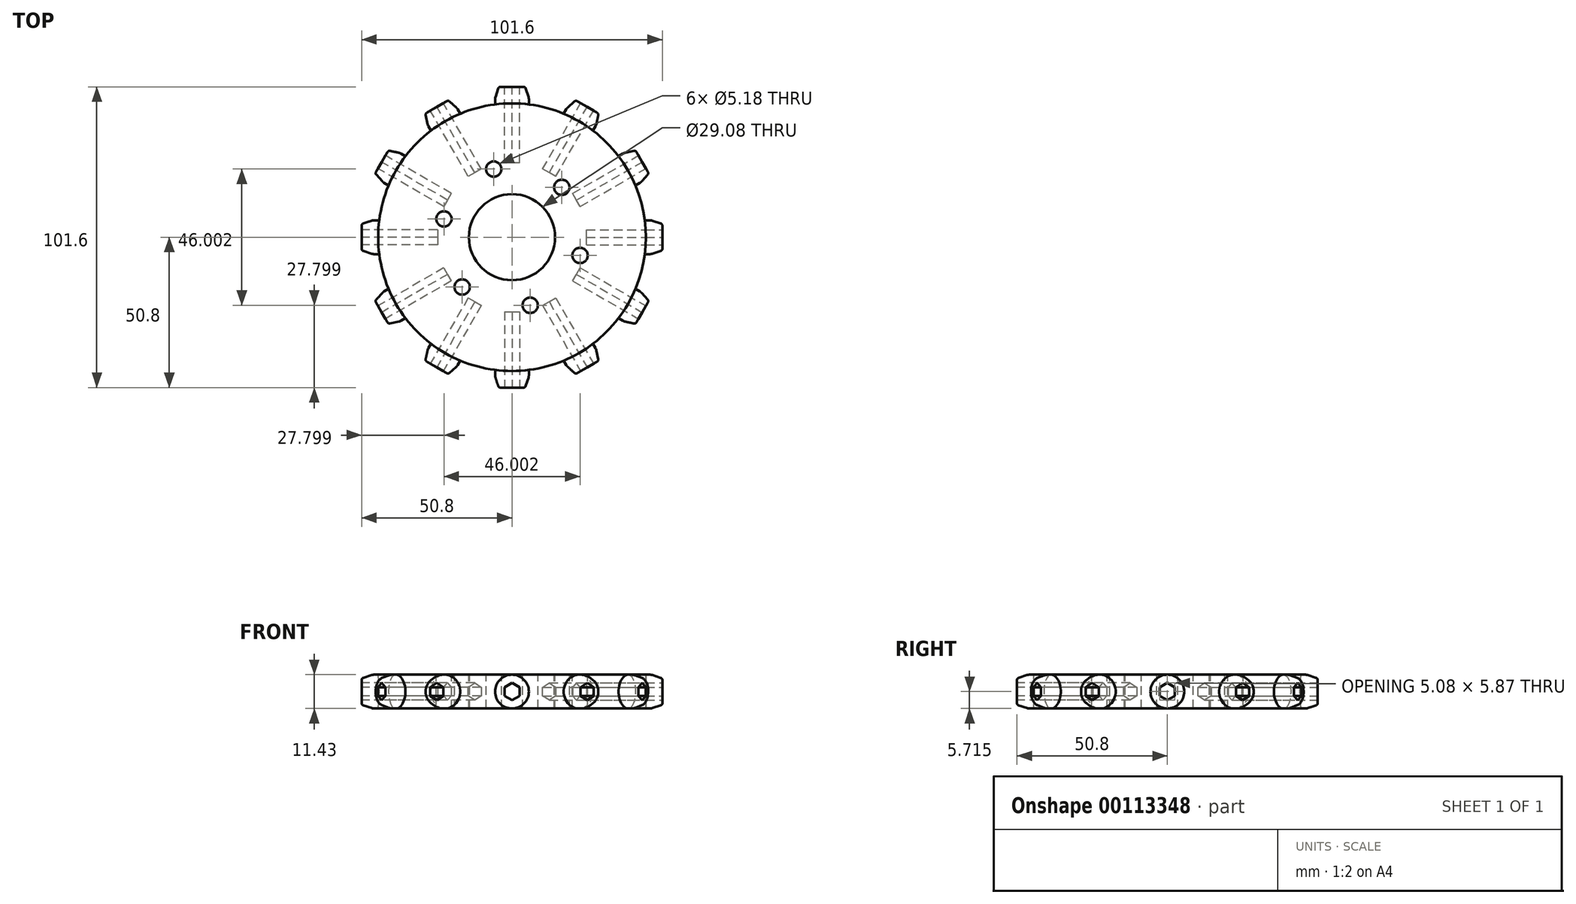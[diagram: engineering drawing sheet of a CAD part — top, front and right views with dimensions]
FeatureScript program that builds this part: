
annotation { "Feature Type Name" : "Feature", "Feature Type Description" : "" }
export const myFeature = defineFeature(function(context is Context, id is Id, definition is map)
    precondition{}
    {
        {
            var Q0;
            Q0=qCreatedBy(makeId("Top.planeOp"),FACE);
            var sketch = newSketch(context, id + "F0", { "sketchPlane" : qUnion([Q0])});
            skCircle(sketch, "E0", {"center": v(0, 0) * mm, "radius": 45.21 * mm});
            skSolve(sketch);
        }
        {
            var Q0;
            Q0=qSketchRegion(id+"F0",true);
            extrude(context, id + "F1", {"entities" : qUnion([Q0]), "depth" : 11.43 * mm});
        }
        {
            var Q0;
            Q0=qCreatedBy(makeId("Front.planeOp"),FACE);
            var sketch = newSketch(context, id + "F2", { "sketchPlane" : qUnion([Q0])});
            skLineSegment(sketch, "E1", {"start": v(0, 0) * mm, "end": v(0, 19.65) * mm, "construction": true});
            skSolve(sketch);
        }
        {
            var Q0;
            Q0=makeQuery(id+"F1.opExtrude","CAP_FACE",FACE,{"disambiguationData":[OSD([sQuery(id+"F0.wireOp",EDGE,"E0")])],"isStart":false});
            var sketch = newSketch(context, id + "F3", { "sketchPlane" : qUnion([Q0])});
            skLineSegment(sketch, "E2", {"start": v(0, 0) * mm, "end": v(0, 60.06) * mm, "construction": true});
            skLineSegment(sketch, "E3", {"start": v(0, 0) * mm, "end": v(-13.99, 52.2) * mm, "construction": true});
            skCircle(sketch, "E4", {"center": v(0, 0) * mm, "radius": 23.81 * mm, "construction": true});
            skCircle(sketch, "E5", {"center": v(-6.16, 23) * mm, "radius": 2.6 * mm});
            skCircle(sketch, "E6.1.0", {"center": v(-23, 6.16) * mm, "radius": 2.6 * mm});
            skCircle(sketch, "E6.2.0", {"center": v(-16.84, -16.84) * mm, "radius": 2.6 * mm});
            skCircle(sketch, "E7.1.3.0", {"center": v(6.16, -23) * mm, "radius": 2.6 * mm});
            skCircle(sketch, "E7.1.4.0", {"center": v(23, -6.16) * mm, "radius": 2.6 * mm});
            skCircle(sketch, "E7.1.5.0", {"center": v(16.84, 16.84) * mm, "radius": 2.6 * mm});
            skLineSegment(sketch, "E8", {"start": v(0, 0) * mm, "end": v(16.84, 16.84) * mm, "construction": true});
            skSolve(sketch);
        }
        {
            var Q0;
            Q0=makeQuery(id+"F3.imprint","IMPRINT",FACE,{"disambiguationData":[TD([[makeQuery(id+"F3.imprint","IMPRINT",EDGE,{"derivedFrom":sQuery(id+"F3.wireOp",EDGE,"E5")}),1.0]])]});
            var Q1;
            Q1=makeQuery(id+"F3.imprint","IMPRINT",FACE,{"disambiguationData":[TD([[makeQuery(id+"F3.imprint","IMPRINT",EDGE,{"derivedFrom":sQuery(id+"F3.wireOp",EDGE,"E6.1.0")}),1.0]])]});
            var Q2;
            Q2=makeQuery(id+"F3.imprint","IMPRINT",FACE,{"disambiguationData":[TD([[makeQuery(id+"F3.imprint","IMPRINT",EDGE,{"derivedFrom":sQuery(id+"F3.wireOp",EDGE,"E6.2.0")}),1.0]])]});
            var Q3;
            Q3=makeQuery(id+"F3.imprint","IMPRINT",FACE,{"disambiguationData":[TD([[makeQuery(id+"F3.imprint","IMPRINT",EDGE,{"derivedFrom":sQuery(id+"F3.wireOp",EDGE,"E7.1.3.0")}),1.0]])]});
            var Q4;
            Q4=makeQuery(id+"F3.imprint","IMPRINT",FACE,{"disambiguationData":[TD([[makeQuery(id+"F3.imprint","IMPRINT",EDGE,{"derivedFrom":sQuery(id+"F3.wireOp",EDGE,"E7.1.4.0")}),1.0]])]});
            var Q5;
            Q5=makeQuery(id+"F3.imprint","IMPRINT",FACE,{"disambiguationData":[TD([[makeQuery(id+"F3.imprint","IMPRINT",EDGE,{"derivedFrom":sQuery(id+"F3.wireOp",EDGE,"E7.1.5.0")}),1.0]])]});
            extrude(context, id + "F4", {"entities" : qUnion([Q0, Q1, Q2, Q3, Q4, Q5]), "operationType" : NewBodyOperationType.REMOVE, "oppositeDirection" : true, "depth" : 25.4 * mm});
        }
        {
            var Q0;
            Q0=makeQuery(id+"F3.imprint","IMPRINT",FACE,{"disambiguationData":[TD([[makeQuery(id+"F3.imprint","IMPRINT",EDGE,{"derivedFrom":sQuery(id+"F3.wireOp",EDGE,"E5")}),-1.0]])]});
            var sketch = newSketch(context, id + "F5", { "sketchPlane" : qUnion([Q0])});
            skCircle(sketch, "E9", {"center": v(0, 0) * mm, "radius": 14.54 * mm});
            skSolve(sketch);
        }
        {
            var Q0;
            Q0=qSketchRegion(id+"F5",true);
            extrude(context, id + "F6", {"entities" : qUnion([Q0]), "operationType" : NewBodyOperationType.REMOVE, "oppositeDirection" : true, "depth" : 25.4 * mm});
        }
        {
            var Q0;
            Q0=qCreatedBy(makeId("Front.planeOp"),FACE);
            cPlane(context, id + "F7", {"entities" : qUnion([Q0]), "cplaneType" : CPlaneType.OFFSET, "offset" : 47 * mm, "oppositeDirection" : true, "width" : 152.4 * mm, "height" : 152.4 * mm});
        }
        {
            var Q0;
            Q0=qCreatedBy(makeId("Top.planeOp"),FACE);
            var sketch = newSketch(context, id + "F8", { "sketchPlane" : qUnion([Q0])});
            skLineSegment(sketch, "E10", {"start": v(0, 0) * mm, "end": v(0, 62.24) * mm, "construction": true});
            skSolve(sketch);
        }
        {
            var Q0;
            Q0=qCreatedBy(id+"F7.planeOp",FACE);
            var sketch = newSketch(context, id + "F9", { "sketchPlane" : qUnion([Q0])});
            skCircle(sketch, "E11", {"center": v(0, 5.72) * mm, "radius": 5.72 * mm});
            skSolve(sketch);
        }
        {
            var Q0;
            Q0 = qSketchRegion(id + "F9", true);
            extrude(context, id + "F10", {"entities" : qUnion([Q0]), "endBound" : BoundingType.UP_TO_NEXT, "depth" : 7.62 * mm, "offsetDistance" : 25.4 * mm});
        }
        {
            var Q0;
            Q0 = qSketchRegion(id + "F9", true);
            extrude(context, id + "F11", {"entities" : qUnion([Q0]), "oppositeDirection" : true, "depth" : 3.8 * mm, "hasDraft" : true, "draftAngle" : 18 * degree, "draftPullDirection" : true, "offsetDistance" : 25.4 * mm});
        }
        {
            var Q0;
            Q0=makeQuery(id+"F11.opExtrude","CAP_FACE",FACE,{"disambiguationData":[OSD([sQuery(id+"F9.wireOp",EDGE,"E11")])],"isStart":false});
            var sketch = newSketch(context, id + "F12", { "sketchPlane" : qUnion([Q0])});
            skCircle(sketch, "E12.cCircle", {"center": v(0, 5.72) * mm, "radius": 2.54 * mm, "construction": true});
            skLineSegment(sketch, "E12.0", {"start": v(2.54, 7.18) * mm, "end": v(2.54, 4.25) * mm});
            skLineSegment(sketch, "E12.1", {"start": v(2.54, 4.25) * mm, "end": v(0, 2.78) * mm});
            skLineSegment(sketch, "E12.2", {"start": v(0, 2.78) * mm, "end": v(-2.54, 4.25) * mm});
            skLineSegment(sketch, "E12.3", {"start": v(-2.54, 4.25) * mm, "end": v(-2.54, 7.18) * mm});
            skLineSegment(sketch, "E12.4", {"start": v(-2.54, 7.18) * mm, "end": v(0, 8.65) * mm});
            skLineSegment(sketch, "E12.5", {"start": v(0, 8.65) * mm, "end": v(2.54, 7.18) * mm});
            skPoint(sketch, "E12.0.midPoint", {"position": v(2.54, 5.72) * mm});
            skSolve(sketch);
        }
        {
            var Q0;
            Q0 = qSketchRegion(id + "F12", true);
            extrude(context, id + "F13", {"entities" : qUnion([Q0]), "operationType" : NewBodyOperationType.REMOVE, "oppositeDirection" : true, "depth" : 25.65 * mm});
        }
        {
            var Q0;
            Q0=makeQuery(id+"F10.opExtrude","SWEPT_BODY",BODY,{"disambiguationData":[OSD([sQuery(id+"F9.wireOp",EDGE,"E11")])]});
            var Q1;
            Q1=makeQuery(id+"F11.opExtrude","SWEPT_BODY",BODY,{"disambiguationData":[OSD([sQuery(id+"F9.wireOp",EDGE,"E11")])]});
            var Q2;
            Q2=sQuery(id+"F2.wireOp",EDGE,"E1");
            circularPattern(context, id + "F14", {"entities" : qUnion([Q0, Q1]), "axis" : qUnion([Q2]), "angle" : 360 * degree, "instanceCount" : 12, "equalSpace" : true});
        }
        {
            var Q0;
            Q0=makeQuery(id+"F10.opExtrude","SWEPT_BODY",BODY,{"disambiguationData":[OSD([sQuery(id+"F9.wireOp",EDGE,"E11")])]});
            var Q1;
            Q1=makeQuery(id+"F11.opExtrude","SWEPT_BODY",BODY,{"disambiguationData":[OSD([sQuery(id+"F9.wireOp",EDGE,"E11")])]});
            var Q2;
            Q2=makeQuery(id+"F14.opPattern","COPY",BODY,{"derivedFrom":makeQuery(id+"F10.opExtrude","SWEPT_BODY",BODY,{"disambiguationData":[OSD([sQuery(id+"F9.wireOp",EDGE,"E11")])]}),"instanceName":"11"});
            var Q3;
            Q3=makeQuery(id+"F14.opPattern","COPY",BODY,{"derivedFrom":makeQuery(id+"F11.opExtrude","SWEPT_BODY",BODY,{"disambiguationData":[OSD([sQuery(id+"F9.wireOp",EDGE,"E11")])]}),"instanceName":"11"});
            var Q4;
            Q4=makeQuery(id+"F14.opPattern","COPY",BODY,{"derivedFrom":makeQuery(id+"F10.opExtrude","SWEPT_BODY",BODY,{"disambiguationData":[OSD([sQuery(id+"F9.wireOp",EDGE,"E11")])]}),"instanceName":"10"});
            var Q5;
            Q5=makeQuery(id+"F14.opPattern","COPY",BODY,{"derivedFrom":makeQuery(id+"F11.opExtrude","SWEPT_BODY",BODY,{"disambiguationData":[OSD([sQuery(id+"F9.wireOp",EDGE,"E11")])]}),"instanceName":"10"});
            var Q6;
            Q6=makeQuery(id+"F14.opPattern","COPY",BODY,{"derivedFrom":makeQuery(id+"F10.opExtrude","SWEPT_BODY",BODY,{"disambiguationData":[OSD([sQuery(id+"F9.wireOp",EDGE,"E11")])]}),"instanceName":"9"});
            var Q7;
            Q7=makeQuery(id+"F14.opPattern","COPY",BODY,{"derivedFrom":makeQuery(id+"F11.opExtrude","SWEPT_BODY",BODY,{"disambiguationData":[OSD([sQuery(id+"F9.wireOp",EDGE,"E11")])]}),"instanceName":"9"});
            var Q8;
            Q8=makeQuery(id+"F14.opPattern","COPY",BODY,{"derivedFrom":makeQuery(id+"F10.opExtrude","SWEPT_BODY",BODY,{"disambiguationData":[OSD([sQuery(id+"F9.wireOp",EDGE,"E11")])]}),"instanceName":"8"});
            var Q9;
            Q9=makeQuery(id+"F14.opPattern","COPY",BODY,{"derivedFrom":makeQuery(id+"F11.opExtrude","SWEPT_BODY",BODY,{"disambiguationData":[OSD([sQuery(id+"F9.wireOp",EDGE,"E11")])]}),"instanceName":"8"});
            booleanBodies(context, id + "F15", {"operationType" : BooleanOperationType.UNION, "tools" : qUnion([Q0, Q1, Q2, Q3, Q4, Q5, Q6, Q7, Q8, Q9])});
        }
        {
            var Q0;
            Q0=makeQuery(id+"F1.opExtrude","SWEPT_BODY",BODY,{"disambiguationData":[OSD([sQuery(id+"F0.wireOp",EDGE,"E0")])]});
            var Q1;
            Q1=makeQuery(id+"F14.opPattern","COPY",BODY,{"derivedFrom":makeQuery(id+"F10.opExtrude","SWEPT_BODY",BODY,{"disambiguationData":[OSD([sQuery(id+"F9.wireOp",EDGE,"E11")])]}),"instanceName":"6"});
            var Q2;
            Q2=makeQuery(id+"F14.opPattern","COPY",BODY,{"derivedFrom":makeQuery(id+"F11.opExtrude","SWEPT_BODY",BODY,{"disambiguationData":[OSD([sQuery(id+"F9.wireOp",EDGE,"E11")])]}),"instanceName":"6"});
            var Q3;
            Q3=makeQuery(id+"F14.opPattern","COPY",BODY,{"derivedFrom":makeQuery(id+"F10.opExtrude","SWEPT_BODY",BODY,{"disambiguationData":[OSD([sQuery(id+"F9.wireOp",EDGE,"E11")])]}),"instanceName":"10"});
            var Q4;
            Q4=makeQuery(id+"F14.opPattern","COPY",BODY,{"derivedFrom":makeQuery(id+"F11.opExtrude","SWEPT_BODY",BODY,{"disambiguationData":[OSD([sQuery(id+"F9.wireOp",EDGE,"E11")])]}),"instanceName":"5"});
            booleanBodies(context, id + "F16", {"operationType" : BooleanOperationType.UNION, "tools" : qUnion([Q0, Q1, Q2, Q3, Q4])});
        }
        {
            var Q0;
            Q0=makeQuery(id+"F1.opExtrude","SWEPT_BODY",BODY,{"disambiguationData":[OSD([sQuery(id+"F0.wireOp",EDGE,"E0")])]});
            var Q1;
            Q1=makeQuery(id+"F14.opPattern","COPY",BODY,{"derivedFrom":makeQuery(id+"F10.opExtrude","SWEPT_BODY",BODY,{"disambiguationData":[OSD([sQuery(id+"F9.wireOp",EDGE,"E11")])]}),"instanceName":"7"});
            var Q2;
            Q2=makeQuery(id+"F14.opPattern","COPY",BODY,{"derivedFrom":makeQuery(id+"F11.opExtrude","SWEPT_BODY",BODY,{"disambiguationData":[OSD([sQuery(id+"F9.wireOp",EDGE,"E11")])]}),"instanceName":"7"});
            var Q3;
            Q3=makeQuery(id+"F14.opPattern","COPY",BODY,{"derivedFrom":makeQuery(id+"F10.opExtrude","SWEPT_BODY",BODY,{"disambiguationData":[OSD([sQuery(id+"F9.wireOp",EDGE,"E11")])]}),"instanceName":"8"});
            booleanBodies(context, id + "F17", {"operationType" : BooleanOperationType.UNION, "tools" : qUnion([Q0, Q1, Q2, Q3])});
        }
        {
            var Q0;
            Q0=makeQuery(id+"F1.opExtrude","SWEPT_BODY",BODY,{"disambiguationData":[OSD([sQuery(id+"F0.wireOp",EDGE,"E0")])]});
            var Q1;
            Q1=makeQuery(id+"F14.opPattern","COPY",BODY,{"derivedFrom":makeQuery(id+"F10.opExtrude","SWEPT_BODY",BODY,{"disambiguationData":[OSD([sQuery(id+"F9.wireOp",EDGE,"E11")])]}),"instanceName":"5"});
            var Q2;
            Q2=makeQuery(id+"F14.opPattern","COPY",BODY,{"derivedFrom":makeQuery(id+"F11.opExtrude","SWEPT_BODY",BODY,{"disambiguationData":[OSD([sQuery(id+"F9.wireOp",EDGE,"E11")])]}),"instanceName":"5"});
            var Q3;
            Q3=makeQuery(id+"F14.opPattern","COPY",BODY,{"derivedFrom":makeQuery(id+"F10.opExtrude","SWEPT_BODY",BODY,{"disambiguationData":[OSD([sQuery(id+"F9.wireOp",EDGE,"E11")])]}),"instanceName":"4"});
            var Q4;
            Q4=makeQuery(id+"F14.opPattern","COPY",BODY,{"derivedFrom":makeQuery(id+"F11.opExtrude","SWEPT_BODY",BODY,{"disambiguationData":[OSD([sQuery(id+"F9.wireOp",EDGE,"E11")])]}),"instanceName":"4"});
            var Q5;
            Q5=makeQuery(id+"F14.opPattern","COPY",BODY,{"derivedFrom":makeQuery(id+"F10.opExtrude","SWEPT_BODY",BODY,{"disambiguationData":[OSD([sQuery(id+"F9.wireOp",EDGE,"E11")])]}),"instanceName":"3"});
            var Q6;
            Q6=makeQuery(id+"F14.opPattern","COPY",BODY,{"derivedFrom":makeQuery(id+"F11.opExtrude","SWEPT_BODY",BODY,{"disambiguationData":[OSD([sQuery(id+"F9.wireOp",EDGE,"E11")])]}),"instanceName":"3"});
            var Q7;
            Q7=makeQuery(id+"F14.opPattern","COPY",BODY,{"derivedFrom":makeQuery(id+"F10.opExtrude","SWEPT_BODY",BODY,{"disambiguationData":[OSD([sQuery(id+"F9.wireOp",EDGE,"E11")])]}),"instanceName":"2"});
            var Q8;
            Q8=makeQuery(id+"F14.opPattern","COPY",BODY,{"derivedFrom":makeQuery(id+"F11.opExtrude","SWEPT_BODY",BODY,{"disambiguationData":[OSD([sQuery(id+"F9.wireOp",EDGE,"E11")])]}),"instanceName":"2"});
            var Q9;
            Q9=makeQuery(id+"F14.opPattern","COPY",BODY,{"derivedFrom":makeQuery(id+"F10.opExtrude","SWEPT_BODY",BODY,{"disambiguationData":[OSD([sQuery(id+"F9.wireOp",EDGE,"E11")])]}),"instanceName":"1"});
            var Q10;
            Q10=makeQuery(id+"F14.opPattern","COPY",BODY,{"derivedFrom":makeQuery(id+"F11.opExtrude","SWEPT_BODY",BODY,{"disambiguationData":[OSD([sQuery(id+"F9.wireOp",EDGE,"E11")])]}),"instanceName":"1"});
            var Q11;
            Q11=makeQuery(id+"F14.opPattern","COPY",BODY,{"derivedFrom":makeQuery(id+"F10.opExtrude","SWEPT_BODY",BODY,{"disambiguationData":[OSD([sQuery(id+"F9.wireOp",EDGE,"E11")])]}),"instanceName":"11"});
            var Q12;
            Q12=makeQuery(id+"F10.opExtrude","SWEPT_BODY",BODY,{"disambiguationData":[OSD([sQuery(id+"F9.wireOp",EDGE,"E11")])]});
            booleanBodies(context, id + "F18", {"operationType" : BooleanOperationType.UNION, "tools" : qUnion([Q0, Q1, Q2, Q3, Q4, Q5, Q6, Q7, Q8, Q9, Q10, Q11, Q12])});
        }
        {
            var Q0;
            {var subQ0=sQuery(id+"F9.wireOp",EDGE,"E11");Q0=makeQuery(id+"F15.opBoolean","MERGE",EDGE,{"derivedFrom":[makeQuery(id+"F10.opExtrude","CAP_EDGE",EDGE,{"disambiguationData":[OSD([subQ0])],"isStart":true}),makeQuery(id+"F11.opExtrude","CAP_EDGE",EDGE,{"disambiguationData":[OSD([subQ0])],"isStart":true})]});}
            var Q1;
            {var subQ0=sQuery(id+"F9.wireOp",EDGE,"E11");Q1=makeQuery(id+"F15.opBoolean","MERGE",EDGE,{"derivedFrom":[makeQuery(id+"F14.opPattern","COPY",EDGE,{"derivedFrom":makeQuery(id+"F10.opExtrude","CAP_EDGE",EDGE,{"disambiguationData":[OSD([subQ0])],"isStart":true}),"instanceName":"11"}),makeQuery(id+"F14.opPattern","COPY",EDGE,{"derivedFrom":makeQuery(id+"F11.opExtrude","CAP_EDGE",EDGE,{"disambiguationData":[OSD([subQ0])],"isStart":true}),"instanceName":"11"})]});}
            var Q2;
            {var subQ0=sQuery(id+"F9.wireOp",EDGE,"E11");Q2=makeQuery(id+"F15.opBoolean","MERGE",EDGE,{"derivedFrom":[makeQuery(id+"F14.opPattern","COPY",EDGE,{"derivedFrom":makeQuery(id+"F10.opExtrude","CAP_EDGE",EDGE,{"disambiguationData":[OSD([subQ0])],"isStart":true}),"instanceName":"10"}),makeQuery(id+"F14.opPattern","COPY",EDGE,{"derivedFrom":makeQuery(id+"F11.opExtrude","CAP_EDGE",EDGE,{"disambiguationData":[OSD([subQ0])],"isStart":true}),"instanceName":"10"})]});}
            var Q3;
            {var subQ0=sQuery(id+"F9.wireOp",EDGE,"E11");Q3=makeQuery(id+"F15.opBoolean","MERGE",EDGE,{"derivedFrom":[makeQuery(id+"F14.opPattern","COPY",EDGE,{"derivedFrom":makeQuery(id+"F10.opExtrude","CAP_EDGE",EDGE,{"disambiguationData":[OSD([subQ0])],"isStart":true}),"instanceName":"9"}),makeQuery(id+"F14.opPattern","COPY",EDGE,{"derivedFrom":makeQuery(id+"F11.opExtrude","CAP_EDGE",EDGE,{"disambiguationData":[OSD([subQ0])],"isStart":true}),"instanceName":"9"})]});}
            var Q4;
            {var subQ0=sQuery(id+"F9.wireOp",EDGE,"E11");Q4=makeQuery(id+"F15.opBoolean","MERGE",EDGE,{"derivedFrom":[makeQuery(id+"F14.opPattern","COPY",EDGE,{"derivedFrom":makeQuery(id+"F10.opExtrude","CAP_EDGE",EDGE,{"disambiguationData":[OSD([subQ0])],"isStart":true}),"instanceName":"8"}),makeQuery(id+"F14.opPattern","COPY",EDGE,{"derivedFrom":makeQuery(id+"F11.opExtrude","CAP_EDGE",EDGE,{"disambiguationData":[OSD([subQ0])],"isStart":true}),"instanceName":"8"})]});}
            var Q5;
            {var subQ0=sQuery(id+"F9.wireOp",EDGE,"E11");Q5=makeQuery(id+"F17.opBoolean","MERGE",EDGE,{"derivedFrom":[makeQuery(id+"F14.opPattern","COPY",EDGE,{"derivedFrom":makeQuery(id+"F10.opExtrude","CAP_EDGE",EDGE,{"disambiguationData":[OSD([subQ0])],"isStart":true}),"instanceName":"7"}),makeQuery(id+"F14.opPattern","COPY",EDGE,{"derivedFrom":makeQuery(id+"F11.opExtrude","CAP_EDGE",EDGE,{"disambiguationData":[OSD([subQ0])],"isStart":true}),"instanceName":"7"})]});}
            var Q6;
            {var subQ0=sQuery(id+"F9.wireOp",EDGE,"E11");Q6=makeQuery(id+"F18.opBoolean","MERGE",EDGE,{"derivedFrom":[makeQuery(id+"F14.opPattern","COPY",EDGE,{"derivedFrom":makeQuery(id+"F10.opExtrude","CAP_EDGE",EDGE,{"disambiguationData":[OSD([subQ0])],"isStart":true}),"instanceName":"1"}),makeQuery(id+"F14.opPattern","COPY",EDGE,{"derivedFrom":makeQuery(id+"F11.opExtrude","CAP_EDGE",EDGE,{"disambiguationData":[OSD([subQ0])],"isStart":true}),"instanceName":"1"})]});}
            var Q7;
            {var subQ0=sQuery(id+"F9.wireOp",EDGE,"E11");Q7=makeQuery(id+"F18.opBoolean","MERGE",EDGE,{"derivedFrom":[makeQuery(id+"F14.opPattern","COPY",EDGE,{"derivedFrom":makeQuery(id+"F10.opExtrude","CAP_EDGE",EDGE,{"disambiguationData":[OSD([subQ0])],"isStart":true}),"instanceName":"2"}),makeQuery(id+"F14.opPattern","COPY",EDGE,{"derivedFrom":makeQuery(id+"F11.opExtrude","CAP_EDGE",EDGE,{"disambiguationData":[OSD([subQ0])],"isStart":true}),"instanceName":"2"})]});}
            var Q8;
            {var subQ0=sQuery(id+"F9.wireOp",EDGE,"E11");Q8=makeQuery(id+"F18.opBoolean","MERGE",EDGE,{"derivedFrom":[makeQuery(id+"F14.opPattern","COPY",EDGE,{"derivedFrom":makeQuery(id+"F10.opExtrude","CAP_EDGE",EDGE,{"disambiguationData":[OSD([subQ0])],"isStart":true}),"instanceName":"3"}),makeQuery(id+"F14.opPattern","COPY",EDGE,{"derivedFrom":makeQuery(id+"F11.opExtrude","CAP_EDGE",EDGE,{"disambiguationData":[OSD([subQ0])],"isStart":true}),"instanceName":"3"})]});}
            var Q9;
            {var subQ0=sQuery(id+"F9.wireOp",EDGE,"E11");Q9=makeQuery(id+"F18.opBoolean","MERGE",EDGE,{"derivedFrom":[makeQuery(id+"F14.opPattern","COPY",EDGE,{"derivedFrom":makeQuery(id+"F10.opExtrude","CAP_EDGE",EDGE,{"disambiguationData":[OSD([subQ0])],"isStart":true}),"instanceName":"4"}),makeQuery(id+"F14.opPattern","COPY",EDGE,{"derivedFrom":makeQuery(id+"F11.opExtrude","CAP_EDGE",EDGE,{"disambiguationData":[OSD([subQ0])],"isStart":true}),"instanceName":"4"})]});}
            var Q10;
            {var subQ0=sQuery(id+"F9.wireOp",EDGE,"E11");Q10=makeQuery(id+"F18.opBoolean","MERGE",EDGE,{"derivedFrom":[makeQuery(id+"F14.opPattern","COPY",EDGE,{"derivedFrom":makeQuery(id+"F10.opExtrude","CAP_EDGE",EDGE,{"disambiguationData":[OSD([subQ0])],"isStart":true}),"instanceName":"5"}),makeQuery(id+"F14.opPattern","COPY",EDGE,{"derivedFrom":makeQuery(id+"F11.opExtrude","CAP_EDGE",EDGE,{"disambiguationData":[OSD([subQ0])],"isStart":true}),"instanceName":"5"})]});}
            var Q11;
            {var subQ0=sQuery(id+"F9.wireOp",EDGE,"E11");Q11=makeQuery(id+"F16.opBoolean","MERGE",EDGE,{"derivedFrom":[makeQuery(id+"F14.opPattern","COPY",EDGE,{"derivedFrom":makeQuery(id+"F10.opExtrude","CAP_EDGE",EDGE,{"disambiguationData":[OSD([subQ0])],"isStart":true}),"instanceName":"6"}),makeQuery(id+"F14.opPattern","COPY",EDGE,{"derivedFrom":makeQuery(id+"F11.opExtrude","CAP_EDGE",EDGE,{"disambiguationData":[OSD([subQ0])],"isStart":true}),"instanceName":"6"})]});}
            fillet(context, id + "F19", {"entities" : qUnion([Q0, Q1, Q2, Q3, Q4, Q5, Q6, Q7, Q8, Q9, Q10, Q11]), "radius" : 2.54 * mm, "tangentPropagation" : true, "allowEdgeOverflow" : false});
        }
        {
            var Q0;
            Q0=makeQuery(id+"F14.opPattern","COPY",FACE,{"derivedFrom":makeQuery(id+"F11.opExtrude","CAP_FACE",FACE,{"disambiguationData":[OSD([sQuery(id+"F9.wireOp",EDGE,"E11")])],"isStart":false}),"instanceName":"1"});
            var sketch = newSketch(context, id + "F20", { "sketchPlane" : qUnion([Q0])});
            skCircle(sketch, "E13.cCircle", {"center": v(0, 5.72) * mm, "radius": 2.54 * mm, "construction": true});
            skLineSegment(sketch, "E13.0", {"start": v(2.54, 7.18) * mm, "end": v(2.54, 4.25) * mm});
            skLineSegment(sketch, "E13.1", {"start": v(2.54, 4.25) * mm, "end": v(0, 2.78) * mm});
            skLineSegment(sketch, "E13.2", {"start": v(0, 2.78) * mm, "end": v(-2.54, 4.25) * mm});
            skLineSegment(sketch, "E13.3", {"start": v(-2.54, 4.25) * mm, "end": v(-2.54, 7.18) * mm});
            skLineSegment(sketch, "E13.4", {"start": v(-2.54, 7.18) * mm, "end": v(0, 8.65) * mm});
            skLineSegment(sketch, "E13.5", {"start": v(0, 8.65) * mm, "end": v(2.54, 7.18) * mm});
            skPoint(sketch, "E13.0.midPoint", {"position": v(2.54, 5.72) * mm});
            skSolve(sketch);
        }
        {
            var Q0;
            Q0 = qSketchRegion(id + "F20", true);
            extrude(context, id + "F21", {"entities" : qUnion([Q0]), "operationType" : NewBodyOperationType.REMOVE, "oppositeDirection" : true, "depth" : 25.65 * mm});
        }
        {
            var Q0;
            Q0=makeQuery(id+"F14.opPattern","COPY",FACE,{"derivedFrom":makeQuery(id+"F11.opExtrude","CAP_FACE",FACE,{"disambiguationData":[OSD([sQuery(id+"F9.wireOp",EDGE,"E11")])],"isStart":false}),"instanceName":"2"});
            var sketch = newSketch(context, id + "F22", { "sketchPlane" : qUnion([Q0])});
            skCircle(sketch, "E14.cCircle", {"center": v(0, 5.72) * mm, "radius": 2.54 * mm, "construction": true});
            skLineSegment(sketch, "E14.0", {"start": v(2.54, 7.18) * mm, "end": v(2.54, 4.25) * mm});
            skLineSegment(sketch, "E14.1", {"start": v(2.54, 4.25) * mm, "end": v(0, 2.78) * mm});
            skLineSegment(sketch, "E14.2", {"start": v(0, 2.78) * mm, "end": v(-2.54, 4.25) * mm});
            skLineSegment(sketch, "E14.3", {"start": v(-2.54, 4.25) * mm, "end": v(-2.54, 7.18) * mm});
            skLineSegment(sketch, "E14.4", {"start": v(-2.54, 7.18) * mm, "end": v(0, 8.65) * mm});
            skLineSegment(sketch, "E14.5", {"start": v(0, 8.65) * mm, "end": v(2.54, 7.18) * mm});
            skPoint(sketch, "E14.0.midPoint", {"position": v(2.54, 5.72) * mm});
            skSolve(sketch);
        }
        {
            var Q0;
            Q0 = qSketchRegion(id + "F22", true);
            extrude(context, id + "F23", {"entities" : qUnion([Q0]), "operationType" : NewBodyOperationType.REMOVE, "oppositeDirection" : true, "depth" : 25.65 * mm});
        }
        {
            var Q0;
            Q0=makeQuery(id+"F14.opPattern","COPY",FACE,{"derivedFrom":makeQuery(id+"F11.opExtrude","CAP_FACE",FACE,{"disambiguationData":[OSD([sQuery(id+"F9.wireOp",EDGE,"E11")])],"isStart":false}),"instanceName":"3"});
            var sketch = newSketch(context, id + "F24", { "sketchPlane" : qUnion([Q0])});
            skCircle(sketch, "E15.cCircle", {"center": v(0, 5.72) * mm, "radius": 2.54 * mm, "construction": true});
            skLineSegment(sketch, "E15.0", {"start": v(2.54, 7.18) * mm, "end": v(2.54, 4.25) * mm});
            skLineSegment(sketch, "E15.1", {"start": v(2.54, 4.25) * mm, "end": v(0, 2.78) * mm});
            skLineSegment(sketch, "E15.2", {"start": v(0, 2.78) * mm, "end": v(-2.54, 4.25) * mm});
            skLineSegment(sketch, "E15.3", {"start": v(-2.54, 4.25) * mm, "end": v(-2.54, 7.18) * mm});
            skLineSegment(sketch, "E15.4", {"start": v(-2.54, 7.18) * mm, "end": v(0, 8.65) * mm});
            skLineSegment(sketch, "E15.5", {"start": v(0, 8.65) * mm, "end": v(2.54, 7.18) * mm});
            skPoint(sketch, "E15.0.midPoint", {"position": v(2.54, 5.72) * mm});
            skSolve(sketch);
        }
        {
            var Q0;
            Q0 = qSketchRegion(id + "F24", true);
            extrude(context, id + "F25", {"entities" : qUnion([Q0]), "operationType" : NewBodyOperationType.REMOVE, "oppositeDirection" : true, "depth" : 25.65 * mm});
        }
        {
            var Q0;
            Q0=makeQuery(id+"F14.opPattern","COPY",FACE,{"derivedFrom":makeQuery(id+"F11.opExtrude","CAP_FACE",FACE,{"disambiguationData":[OSD([sQuery(id+"F9.wireOp",EDGE,"E11")])],"isStart":false}),"instanceName":"4"});
            var sketch = newSketch(context, id + "F26", { "sketchPlane" : qUnion([Q0])});
            skCircle(sketch, "E16.cCircle", {"center": v(0, 5.72) * mm, "radius": 2.54 * mm, "construction": true});
            skLineSegment(sketch, "E16.0", {"start": v(2.54, 7.18) * mm, "end": v(2.54, 4.25) * mm});
            skLineSegment(sketch, "E16.1", {"start": v(2.54, 4.25) * mm, "end": v(0, 2.78) * mm});
            skLineSegment(sketch, "E16.2", {"start": v(0, 2.78) * mm, "end": v(-2.54, 4.25) * mm});
            skLineSegment(sketch, "E16.3", {"start": v(-2.54, 4.25) * mm, "end": v(-2.54, 7.18) * mm});
            skLineSegment(sketch, "E16.4", {"start": v(-2.54, 7.18) * mm, "end": v(0, 8.65) * mm});
            skLineSegment(sketch, "E16.5", {"start": v(0, 8.65) * mm, "end": v(2.54, 7.18) * mm});
            skPoint(sketch, "E16.0.midPoint", {"position": v(2.54, 5.72) * mm});
            skSolve(sketch);
        }
        {
            var Q0;
            Q0 = qSketchRegion(id + "F26", true);
            extrude(context, id + "F27", {"entities" : qUnion([Q0]), "operationType" : NewBodyOperationType.REMOVE, "oppositeDirection" : true, "depth" : 25.65 * mm});
        }
        {
            var Q0;
            Q0=makeQuery(id+"F14.opPattern","COPY",FACE,{"derivedFrom":makeQuery(id+"F11.opExtrude","CAP_FACE",FACE,{"disambiguationData":[OSD([sQuery(id+"F9.wireOp",EDGE,"E11")])],"isStart":false}),"instanceName":"5"});
            var sketch = newSketch(context, id + "F28", { "sketchPlane" : qUnion([Q0])});
            skCircle(sketch, "E17.cCircle", {"center": v(0, 5.71) * mm, "radius": 2.54 * mm, "construction": true});
            skLineSegment(sketch, "E17.0", {"start": v(2.54, 7.18) * mm, "end": v(2.54, 4.25) * mm});
            skLineSegment(sketch, "E17.1", {"start": v(2.54, 4.25) * mm, "end": v(0, 2.78) * mm});
            skLineSegment(sketch, "E17.2", {"start": v(0, 2.78) * mm, "end": v(-2.54, 4.25) * mm});
            skLineSegment(sketch, "E17.3", {"start": v(-2.54, 4.25) * mm, "end": v(-2.54, 7.18) * mm});
            skLineSegment(sketch, "E17.4", {"start": v(-2.54, 7.18) * mm, "end": v(0, 8.65) * mm});
            skLineSegment(sketch, "E17.5", {"start": v(0, 8.65) * mm, "end": v(2.54, 7.18) * mm});
            skPoint(sketch, "E17.0.midPoint", {"position": v(2.54, 5.71) * mm});
            skSolve(sketch);
        }
        {
            var Q0;
            Q0 = qSketchRegion(id + "F28", true);
            extrude(context, id + "F29", {"entities" : qUnion([Q0]), "operationType" : NewBodyOperationType.REMOVE, "oppositeDirection" : true, "depth" : 25.65 * mm});
        }
        {
            var Q0;
            Q0=makeQuery(id+"F14.opPattern","COPY",FACE,{"derivedFrom":makeQuery(id+"F11.opExtrude","CAP_FACE",FACE,{"disambiguationData":[OSD([sQuery(id+"F9.wireOp",EDGE,"E11")])],"isStart":false}),"instanceName":"6"});
            var sketch = newSketch(context, id + "F30", { "sketchPlane" : qUnion([Q0])});
            skCircle(sketch, "E18.cCircle", {"center": v(0, 5.72) * mm, "radius": 2.54 * mm, "construction": true});
            skLineSegment(sketch, "E18.0", {"start": v(2.54, 7.18) * mm, "end": v(2.54, 4.25) * mm});
            skLineSegment(sketch, "E18.1", {"start": v(2.54, 4.25) * mm, "end": v(0, 2.78) * mm});
            skLineSegment(sketch, "E18.2", {"start": v(0, 2.78) * mm, "end": v(-2.54, 4.25) * mm});
            skLineSegment(sketch, "E18.3", {"start": v(-2.54, 4.25) * mm, "end": v(-2.54, 7.18) * mm});
            skLineSegment(sketch, "E18.4", {"start": v(-2.54, 7.18) * mm, "end": v(0, 8.65) * mm});
            skLineSegment(sketch, "E18.5", {"start": v(0, 8.65) * mm, "end": v(2.54, 7.18) * mm});
            skPoint(sketch, "E18.0.midPoint", {"position": v(2.54, 5.72) * mm});
            skSolve(sketch);
        }
        {
            var Q0;
            Q0 = qSketchRegion(id + "F30", true);
            extrude(context, id + "F31", {"entities" : qUnion([Q0]), "operationType" : NewBodyOperationType.REMOVE, "oppositeDirection" : true, "depth" : 25.65 * mm});
        }
        {
            var Q0;
            Q0=makeQuery(id+"F14.opPattern","COPY",FACE,{"derivedFrom":makeQuery(id+"F11.opExtrude","CAP_FACE",FACE,{"disambiguationData":[OSD([sQuery(id+"F9.wireOp",EDGE,"E11")])],"isStart":false}),"instanceName":"7"});
            var sketch = newSketch(context, id + "F32", { "sketchPlane" : qUnion([Q0])});
            skCircle(sketch, "E19.cCircle", {"center": v(0, 5.72) * mm, "radius": 2.54 * mm, "construction": true});
            skLineSegment(sketch, "E19.0", {"start": v(2.54, 7.18) * mm, "end": v(2.54, 4.25) * mm});
            skLineSegment(sketch, "E19.1", {"start": v(2.54, 4.25) * mm, "end": v(0, 2.78) * mm});
            skLineSegment(sketch, "E19.2", {"start": v(0, 2.78) * mm, "end": v(-2.54, 4.25) * mm});
            skLineSegment(sketch, "E19.3", {"start": v(-2.54, 4.25) * mm, "end": v(-2.54, 7.18) * mm});
            skLineSegment(sketch, "E19.4", {"start": v(-2.54, 7.18) * mm, "end": v(0, 8.65) * mm});
            skLineSegment(sketch, "E19.5", {"start": v(0, 8.65) * mm, "end": v(2.54, 7.18) * mm});
            skPoint(sketch, "E19.0.midPoint", {"position": v(2.54, 5.72) * mm});
            skSolve(sketch);
        }
        {
            var Q0;
            Q0 = qSketchRegion(id + "F32", true);
            extrude(context, id + "F33", {"entities" : qUnion([Q0]), "operationType" : NewBodyOperationType.REMOVE, "oppositeDirection" : true, "depth" : 25.65 * mm});
        }
        {
            var Q0;
            Q0=makeQuery(id+"F14.opPattern","COPY",FACE,{"derivedFrom":makeQuery(id+"F11.opExtrude","CAP_FACE",FACE,{"disambiguationData":[OSD([sQuery(id+"F9.wireOp",EDGE,"E11")])],"isStart":false}),"instanceName":"8"});
            var sketch = newSketch(context, id + "F34", { "sketchPlane" : qUnion([Q0])});
            skCircle(sketch, "E20.cCircle", {"center": v(0, 5.72) * mm, "radius": 2.54 * mm, "construction": true});
            skLineSegment(sketch, "E20.0", {"start": v(2.54, 7.18) * mm, "end": v(2.54, 4.25) * mm});
            skLineSegment(sketch, "E20.1", {"start": v(2.54, 4.25) * mm, "end": v(0, 2.78) * mm});
            skLineSegment(sketch, "E20.2", {"start": v(0, 2.78) * mm, "end": v(-2.54, 4.25) * mm});
            skLineSegment(sketch, "E20.3", {"start": v(-2.54, 4.25) * mm, "end": v(-2.54, 7.18) * mm});
            skLineSegment(sketch, "E20.4", {"start": v(-2.54, 7.18) * mm, "end": v(0, 8.65) * mm});
            skLineSegment(sketch, "E20.5", {"start": v(0, 8.65) * mm, "end": v(2.54, 7.18) * mm});
            skPoint(sketch, "E20.0.midPoint", {"position": v(2.54, 5.72) * mm});
            skSolve(sketch);
        }
        {
            var Q0;
            Q0 = qSketchRegion(id + "F34", true);
            extrude(context, id + "F35", {"entities" : qUnion([Q0]), "operationType" : NewBodyOperationType.REMOVE, "oppositeDirection" : true, "depth" : 25.65 * mm});
        }
        {
            var Q0;
            Q0=makeQuery(id+"F14.opPattern","COPY",FACE,{"derivedFrom":makeQuery(id+"F11.opExtrude","CAP_FACE",FACE,{"disambiguationData":[OSD([sQuery(id+"F9.wireOp",EDGE,"E11")])],"isStart":false}),"instanceName":"9"});
            var sketch = newSketch(context, id + "F36", { "sketchPlane" : qUnion([Q0])});
            skCircle(sketch, "E21.cCircle", {"center": v(0, 5.72) * mm, "radius": 2.54 * mm, "construction": true});
            skLineSegment(sketch, "E21.0", {"start": v(2.54, 7.18) * mm, "end": v(2.54, 4.25) * mm});
            skLineSegment(sketch, "E21.1", {"start": v(2.54, 4.25) * mm, "end": v(0, 2.78) * mm});
            skLineSegment(sketch, "E21.2", {"start": v(0, 2.78) * mm, "end": v(-2.54, 4.25) * mm});
            skLineSegment(sketch, "E21.3", {"start": v(-2.54, 4.25) * mm, "end": v(-2.54, 7.18) * mm});
            skLineSegment(sketch, "E21.4", {"start": v(-2.54, 7.18) * mm, "end": v(0, 8.65) * mm});
            skLineSegment(sketch, "E21.5", {"start": v(0, 8.65) * mm, "end": v(2.54, 7.18) * mm});
            skPoint(sketch, "E21.0.midPoint", {"position": v(2.54, 5.72) * mm});
            skSolve(sketch);
        }
        {
            var Q0;
            Q0 = qSketchRegion(id + "F36", true);
            extrude(context, id + "F37", {"entities" : qUnion([Q0]), "operationType" : NewBodyOperationType.REMOVE, "oppositeDirection" : true, "depth" : 25.65 * mm});
        }
        {
            var Q0;
            Q0=makeQuery(id+"F14.opPattern","COPY",FACE,{"derivedFrom":makeQuery(id+"F11.opExtrude","CAP_FACE",FACE,{"disambiguationData":[OSD([sQuery(id+"F9.wireOp",EDGE,"E11")])],"isStart":false}),"instanceName":"10"});
            var sketch = newSketch(context, id + "F38", { "sketchPlane" : qUnion([Q0])});
            skCircle(sketch, "E22.cCircle", {"center": v(0, 5.72) * mm, "radius": 2.54 * mm, "construction": true});
            skLineSegment(sketch, "E22.0", {"start": v(2.54, 7.18) * mm, "end": v(2.54, 4.25) * mm});
            skLineSegment(sketch, "E22.1", {"start": v(2.54, 4.25) * mm, "end": v(0, 2.78) * mm});
            skLineSegment(sketch, "E22.2", {"start": v(0, 2.78) * mm, "end": v(-2.54, 4.25) * mm});
            skLineSegment(sketch, "E22.3", {"start": v(-2.54, 4.25) * mm, "end": v(-2.54, 7.18) * mm});
            skLineSegment(sketch, "E22.4", {"start": v(-2.54, 7.18) * mm, "end": v(0, 8.65) * mm});
            skLineSegment(sketch, "E22.5", {"start": v(0, 8.65) * mm, "end": v(2.54, 7.18) * mm});
            skPoint(sketch, "E22.0.midPoint", {"position": v(2.54, 5.72) * mm});
            skSolve(sketch);
        }
        {
            var Q0;
            Q0 = qSketchRegion(id + "F38", true);
            extrude(context, id + "F39", {"entities" : qUnion([Q0]), "operationType" : NewBodyOperationType.REMOVE, "oppositeDirection" : true, "depth" : 25.65 * mm});
        }
        {
            var Q0;
            Q0=makeQuery(id+"F14.opPattern","COPY",FACE,{"derivedFrom":makeQuery(id+"F11.opExtrude","CAP_FACE",FACE,{"disambiguationData":[OSD([sQuery(id+"F9.wireOp",EDGE,"E11")])],"isStart":false}),"instanceName":"11"});
            var sketch = newSketch(context, id + "F40", { "sketchPlane" : qUnion([Q0])});
            skCircle(sketch, "E23.cCircle", {"center": v(0, 5.72) * mm, "radius": 2.54 * mm, "construction": true});
            skLineSegment(sketch, "E23.0", {"start": v(2.54, 7.18) * mm, "end": v(2.54, 4.25) * mm});
            skLineSegment(sketch, "E23.1", {"start": v(2.54, 4.25) * mm, "end": v(0, 2.78) * mm});
            skLineSegment(sketch, "E23.2", {"start": v(0, 2.78) * mm, "end": v(-2.54, 4.25) * mm});
            skLineSegment(sketch, "E23.3", {"start": v(-2.54, 4.25) * mm, "end": v(-2.54, 7.18) * mm});
            skLineSegment(sketch, "E23.4", {"start": v(-2.54, 7.18) * mm, "end": v(0, 8.65) * mm});
            skLineSegment(sketch, "E23.5", {"start": v(0, 8.65) * mm, "end": v(2.54, 7.18) * mm});
            skPoint(sketch, "E23.0.midPoint", {"position": v(2.54, 5.72) * mm});
            skSolve(sketch);
        }
        {
            var Q0;
            Q0 = qSketchRegion(id + "F40", true);
            extrude(context, id + "F41", {"entities" : qUnion([Q0]), "operationType" : NewBodyOperationType.REMOVE, "oppositeDirection" : true, "depth" : 25.65 * mm});
        }
        {
            var Q0;
            Q0=makeQuery(id+"F14.opPattern","COPY",EDGE,{"derivedFrom":makeQuery(id+"F11.opExtrude","CAP_EDGE",EDGE,{"disambiguationData":[OSD([sQuery(id+"F9.wireOp",EDGE,"E11")])],"isStart":false}),"instanceName":"3"});
            var Q1;
            Q1=makeQuery(id+"F14.opPattern","COPY",EDGE,{"derivedFrom":makeQuery(id+"F11.opExtrude","CAP_EDGE",EDGE,{"disambiguationData":[OSD([sQuery(id+"F9.wireOp",EDGE,"E11")])],"isStart":false}),"instanceName":"4"});
            var Q2;
            Q2=makeQuery(id+"F14.opPattern","COPY",EDGE,{"derivedFrom":makeQuery(id+"F11.opExtrude","CAP_EDGE",EDGE,{"disambiguationData":[OSD([sQuery(id+"F9.wireOp",EDGE,"E11")])],"isStart":false}),"instanceName":"5"});
            var Q3;
            Q3=makeQuery(id+"F14.opPattern","COPY",EDGE,{"derivedFrom":makeQuery(id+"F11.opExtrude","CAP_EDGE",EDGE,{"disambiguationData":[OSD([sQuery(id+"F9.wireOp",EDGE,"E11")])],"isStart":false}),"instanceName":"2"});
            var Q4;
            Q4=makeQuery(id+"F14.opPattern","COPY",EDGE,{"derivedFrom":makeQuery(id+"F11.opExtrude","CAP_EDGE",EDGE,{"disambiguationData":[OSD([sQuery(id+"F9.wireOp",EDGE,"E11")])],"isStart":false}),"instanceName":"1"});
            var Q5;
            Q5=makeQuery(id+"F11.opExtrude","CAP_EDGE",EDGE,{"disambiguationData":[OSD([sQuery(id+"F9.wireOp",EDGE,"E11")])],"isStart":false});
            var Q6;
            Q6=makeQuery(id+"F14.opPattern","COPY",EDGE,{"derivedFrom":makeQuery(id+"F11.opExtrude","CAP_EDGE",EDGE,{"disambiguationData":[OSD([sQuery(id+"F9.wireOp",EDGE,"E11")])],"isStart":false}),"instanceName":"11"});
            var Q7;
            Q7=makeQuery(id+"F14.opPattern","COPY",EDGE,{"derivedFrom":makeQuery(id+"F11.opExtrude","CAP_EDGE",EDGE,{"disambiguationData":[OSD([sQuery(id+"F9.wireOp",EDGE,"E11")])],"isStart":false}),"instanceName":"10"});
            var Q8;
            Q8=makeQuery(id+"F14.opPattern","COPY",EDGE,{"derivedFrom":makeQuery(id+"F11.opExtrude","CAP_EDGE",EDGE,{"disambiguationData":[OSD([sQuery(id+"F9.wireOp",EDGE,"E11")])],"isStart":false}),"instanceName":"9"});
            var Q9;
            Q9=makeQuery(id+"F14.opPattern","COPY",EDGE,{"derivedFrom":makeQuery(id+"F11.opExtrude","CAP_EDGE",EDGE,{"disambiguationData":[OSD([sQuery(id+"F9.wireOp",EDGE,"E11")])],"isStart":false}),"instanceName":"8"});
            var Q10;
            Q10=makeQuery(id+"F14.opPattern","COPY",EDGE,{"derivedFrom":makeQuery(id+"F11.opExtrude","CAP_EDGE",EDGE,{"disambiguationData":[OSD([sQuery(id+"F9.wireOp",EDGE,"E11")])],"isStart":false}),"instanceName":"7"});
            var Q11;
            Q11=makeQuery(id+"F14.opPattern","COPY",EDGE,{"derivedFrom":makeQuery(id+"F11.opExtrude","CAP_EDGE",EDGE,{"disambiguationData":[OSD([sQuery(id+"F9.wireOp",EDGE,"E11")])],"isStart":false}),"instanceName":"6"});
            fillet(context, id + "F42", {"entities" : qUnion([Q0, Q1, Q2, Q3, Q4, Q5, Q6, Q7, Q8, Q9, Q10, Q11]), "radius" : 0.76 * mm, "tangentPropagation" : true, "allowEdgeOverflow" : false});
        }
    });
